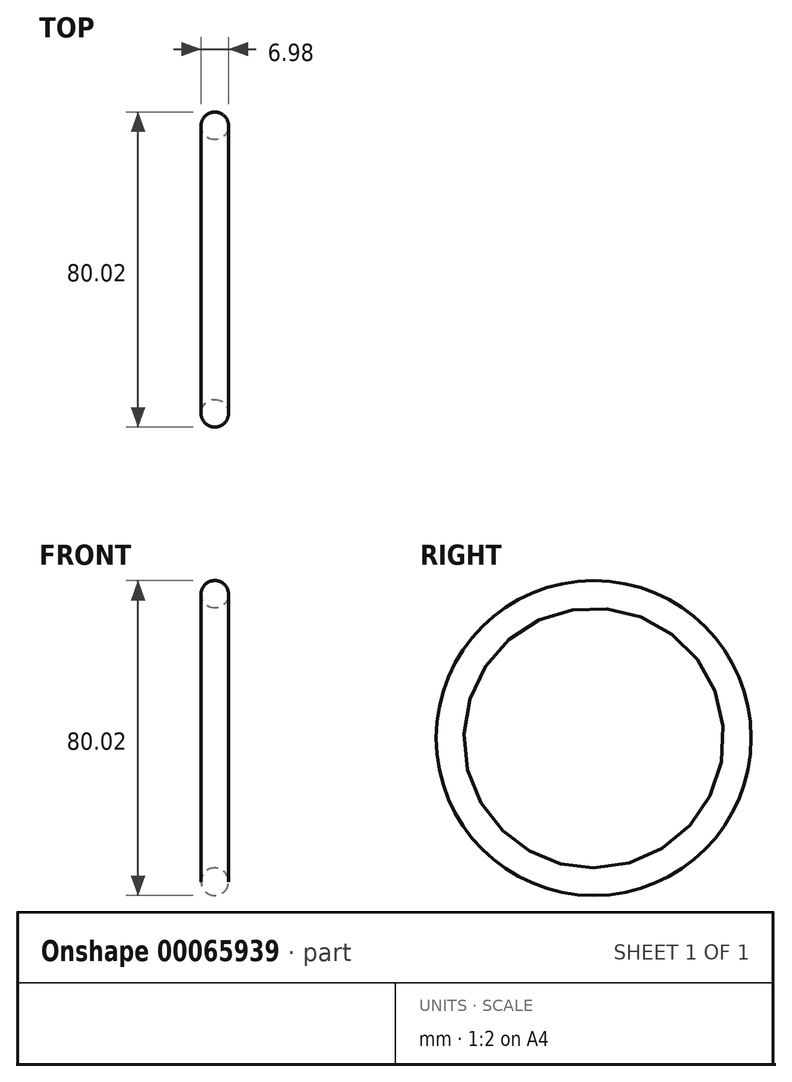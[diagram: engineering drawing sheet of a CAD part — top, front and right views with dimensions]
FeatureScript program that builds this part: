
annotation { "Feature Type Name" : "Feature", "Feature Type Description" : "" }
export const myFeature = defineFeature(function(context is Context, id is Id, definition is map)
    precondition{}
    {
        {
            var Q0;
            Q0=qCreatedBy(makeId("Front.planeOp"),FACE);
            var sketch = newSketch(context, id + "F0", { "sketchPlane" : qUnion([Q0])});
            skLineSegment(sketch, "E0", {"start": v(0, 0) * mm, "end": v(-6.06, 0) * mm, "construction": true});
            skCircle(sketch, "E1", {"center": v(0, 36.51) * mm, "radius": 3.5 * mm});
            skSolve(sketch);
        }
        {
            var Q0;
            Q0=makeQuery(id+"F0.imprint","IMPRINT",FACE,{"disambiguationData":[TD([[makeQuery(id+"F0.imprint","IMPRINT",EDGE,{"derivedFrom":sQuery(id+"F0.wireOp",EDGE,"E1")}),1.0]])]});
            var Q1;
            Q1=sQuery(id+"F0.wireOp",EDGE,"E0");
            revolve(context, id + "F1", {"entities" : qUnion([Q0]), "axis" : qUnion([Q1]), "revolveType" : RevolveType.FULL});
        }
    });
